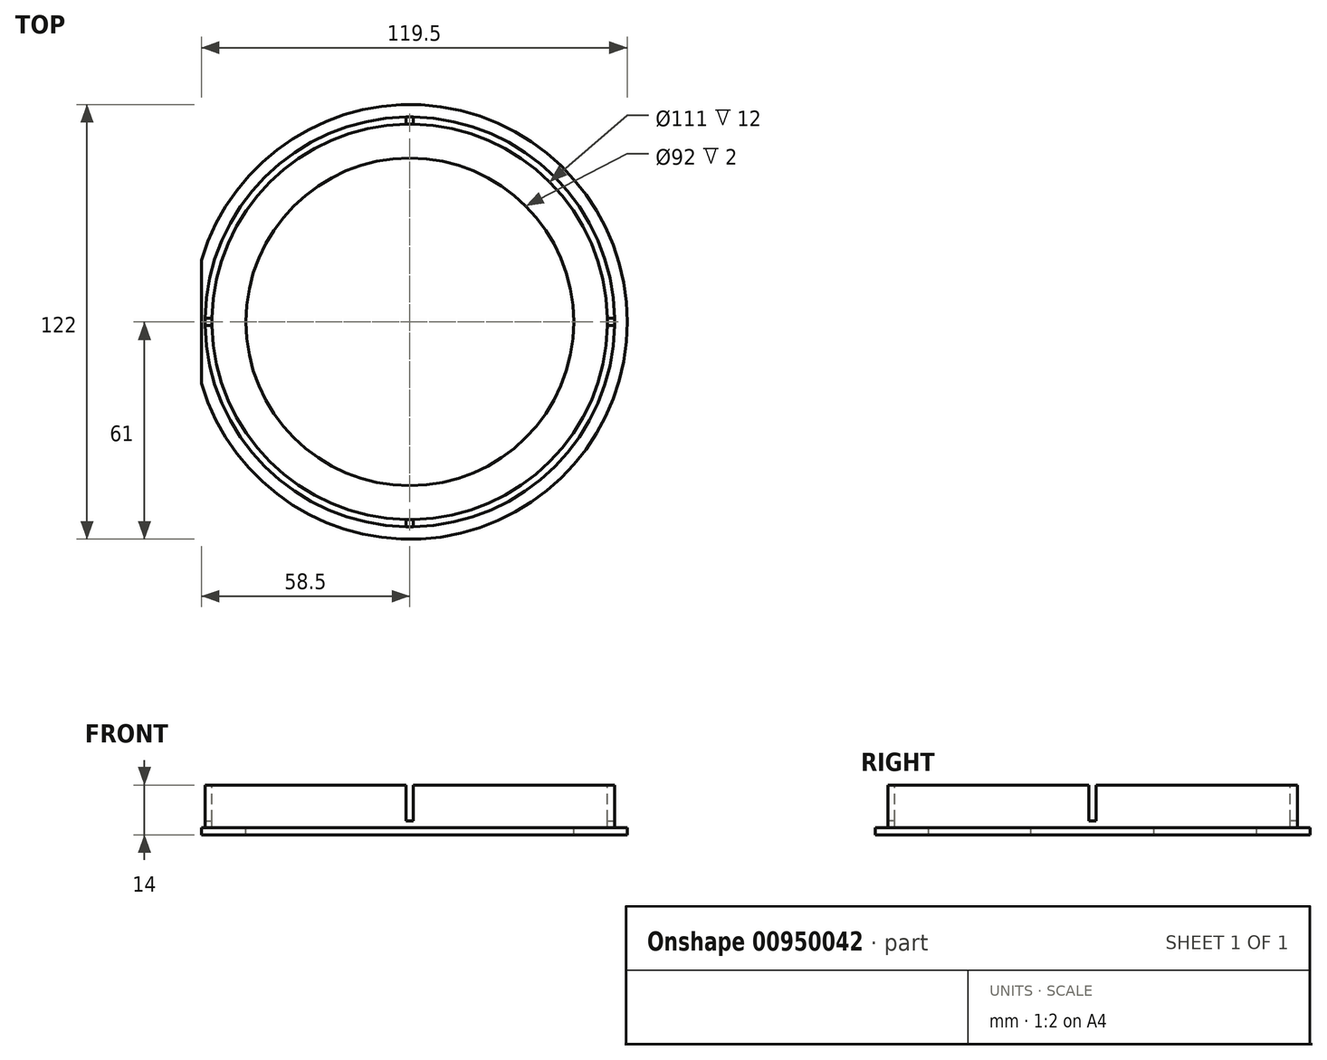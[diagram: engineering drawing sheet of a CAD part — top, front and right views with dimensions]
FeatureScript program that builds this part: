
annotation { "Feature Type Name" : "Feature", "Feature Type Description" : "" }
export const myFeature = defineFeature(function(context is Context, id is Id, definition is map)
    precondition{}
    {
        {
            var Q0;
            Q0=qCreatedBy(makeId("Top.planeOp"),FACE);
            var sketch = newSketch(context, id + "F0", { "sketchPlane" : qUnion([Q0])});
            skCircle(sketch, "E0", {"center": v(0, 0) * mm, "radius": 61 * mm});
            skSolve(sketch);
        }
        {
            var Q0;
            Q0=makeQuery(id+"F0.imprint","IMPRINT",FACE,{"disambiguationData":[TD([[makeQuery(id+"F0.imprint","IMPRINT",EDGE,{"derivedFrom":sQuery(id+"F0.wireOp",EDGE,"E0")}),1.0]])]});
            extrude(context, id + "F1", {"entities" : qUnion([Q0]), "depth" : 2 * mm, "offsetDistance" : 25 * mm});
        }
        {
            var Q0;
            Q0=makeQuery(id+"F1.opExtrude","CAP_FACE",FACE,{"disambiguationData":[OSD([sQuery(id+"F0.wireOp",EDGE,"E0")])],"isStart":false});
            var sketch = newSketch(context, id + "F2", { "sketchPlane" : qUnion([Q0])});
            skCircle(sketch, "E1", {"center": v(0, 0) * mm, "radius": 57.5 * mm});
            skSolve(sketch);
        }
        {
            var Q0;
            Q0=makeQuery(id+"F2.imprint","IMPRINT",FACE,{"disambiguationData":[TD([[makeQuery(id+"F2.imprint","IMPRINT",EDGE,{"derivedFrom":sQuery(id+"F2.wireOp",EDGE,"E1")}),1.0]])]});
            extrude(context, id + "F3", {"entities" : qUnion([Q0]), "operationType" : NewBodyOperationType.ADD, "depth" : 12 * mm, "offsetDistance" : 25 * mm});
        }
        {
            var Q0;
            Q0=makeQuery(id+"F3.opExtrude","CAP_FACE",FACE,{"disambiguationData":[OSD([sQuery(id+"F2.wireOp",EDGE,"E1")])],"isStart":false});
            var sketch = newSketch(context, id + "F4", { "sketchPlane" : qUnion([Q0])});
            skCircle(sketch, "E2", {"center": v(0, 0) * mm, "radius": 46 * mm});
            skSolve(sketch);
        }
        {
            var Q0;
            Q0=makeQuery(id+"F4.imprint","IMPRINT",FACE,{"disambiguationData":[TD([[makeQuery(id+"F4.imprint","IMPRINT",EDGE,{"derivedFrom":sQuery(id+"F4.wireOp",EDGE,"E2")}),1.0]])]});
            extrude(context, id + "F5", {"entities" : qUnion([Q0]), "operationType" : NewBodyOperationType.REMOVE, "oppositeDirection" : true, "depth" : 112.4 * mm, "offsetDistance" : 25 * mm});
        }
        {
            var Q0;
            Q0=makeQuery(id+"F3.opExtrude","CAP_FACE",FACE,{"disambiguationData":[OSD([sQuery(id+"F2.wireOp",EDGE,"E1")])],"isStart":false});
            var sketch = newSketch(context, id + "F6", { "sketchPlane" : qUnion([Q0])});
            skCircle(sketch, "E3", {"center": v(0, 0) * mm, "radius": 55.5 * mm});
            skSolve(sketch);
        }
        {
            var Q0;
            Q0=makeQuery(id+"F6.imprint","IMPRINT",FACE,{"disambiguationData":[TD([[makeQuery(id+"F6.imprint","IMPRINT",EDGE,{"derivedFrom":sQuery(id+"F6.wireOp",EDGE,"E3")}),1.0]])]});
            extrude(context, id + "F7", {"entities" : qUnion([Q0]), "operationType" : NewBodyOperationType.REMOVE, "oppositeDirection" : true, "depth" : 12 * mm, "offsetDistance" : 25 * mm});
        }
        {
            var Q0;
            Q0=makeQuery(id+"F1.opExtrude","CAP_FACE",FACE,{"disambiguationData":[OSD([sQuery(id+"F0.wireOp",EDGE,"E0")])],"isStart":false});
            var sketch = newSketch(context, id + "F8", { "sketchPlane" : qUnion([Q0])});
            skLineSegment(sketch, "E4.bottom", {"start": v(-58.5, 24.5) * mm, "end": v(58.5, 24.5) * mm});
            skLineSegment(sketch, "E4.top", {"start": v(-58.5, -24.5) * mm, "end": v(58.5, -24.5) * mm});
            skLineSegment(sketch, "E4.left", {"start": v(-58.5, 24.5) * mm, "end": v(-58.5, -24.5) * mm});
            skLineSegment(sketch, "E4.right", {"start": v(58.5, 24.5) * mm, "end": v(58.5, -24.5) * mm});
            skPoint(sketch, "E4.middle", {"position": v(0, 0) * mm});
            skSolve(sketch);
        }
        {
            var Q0;
            {var subQ0=sQuery(id+"F8.wireOp",EDGE,"E4.left");var subQ1=makeQuery(id+"F1.opExtrude","CAP_EDGE",EDGE,{"disambiguationData":[OSD([sQuery(id+"F0.wireOp",EDGE,"E0")])],"isStart":false});var subQ2=makeQuery(id+"F8.imprint","INTERSECT",VERTEX,{"disambiguationData":[OD(0.0)],"derivedFrom":[subQ1,subQ0]});Q0=makeQuery(id+"F8.imprint","IMPRINT",FACE,{"disambiguationData":[TD([[makeQuery(id+"F8.imprint","IMPRINT",EDGE,{"disambiguationData":[TD([[subQ2,-1.0]])],"derivedFrom":subQ0}),-1.0]])]});}
            extrude(context, id + "F9", {"entities" : qUnion([Q0]), "operationType" : NewBodyOperationType.REMOVE, "oppositeDirection" : true, "depth" : 25 * mm, "offsetDistance" : 25 * mm});
        }
        {
            var Q0;
            Q0=makeQuery(id+"F3.opExtrude","CAP_FACE",FACE,{"disambiguationData":[OSD([sQuery(id+"F2.wireOp",EDGE,"E1")])],"isStart":false});
            var sketch = newSketch(context, id + "F10", { "sketchPlane" : qUnion([Q0])});
            skLineSegment(sketch, "E5.bottom", {"start": v(-65.22, 1) * mm, "end": v(65.22, 1) * mm});
            skLineSegment(sketch, "E5.top", {"start": v(-65.22, -1) * mm, "end": v(65.22, -1) * mm});
            skLineSegment(sketch, "E5.left", {"start": v(-65.22, 1) * mm, "end": v(-65.22, -1) * mm});
            skLineSegment(sketch, "E5.right", {"start": v(65.22, 1) * mm, "end": v(65.22, -1) * mm});
            skPoint(sketch, "E5.middle", {"position": v(0, 0) * mm});
            skSolve(sketch);
        }
        {
            var Q0;
            Q0 = qSketchRegion(id + "F10", true);
            extrude(context, id + "F11", {"entities" : qUnion([Q0]), "operationType" : NewBodyOperationType.REMOVE, "oppositeDirection" : true, "depth" : 10 * mm, "offsetDistance" : 25 * mm});
        }
        {
            var Q0;
            {var subQ0=sQuery(id+"F2.wireOp",EDGE,"E1");Q0=makeQuery(id+"F11.boolean.opBoolean","SPLIT",FACE,{"disambiguationData":[TD([makeQuery(id+"F11.opExtrude","SWEPT_FACE",FACE,{"disambiguationData":[OSD([sQuery(id+"F10.wireOp",EDGE,"E5.bottom")])]})])],"derivedFrom":makeQuery(id+"F3.opExtrude","CAP_FACE",FACE,{"disambiguationData":[OSD([subQ0])],"isStart":false})});}
            var sketch = newSketch(context, id + "F12", { "sketchPlane" : qUnion([Q0])});
            skLineSegment(sketch, "E6.bottom", {"start": v(-1, 59.5) * mm, "end": v(1, 59.5) * mm});
            skLineSegment(sketch, "E6.top", {"start": v(-1, -59.5) * mm, "end": v(1, -59.5) * mm});
            skLineSegment(sketch, "E6.left", {"start": v(-1, 59.5) * mm, "end": v(-1, -59.5) * mm});
            skLineSegment(sketch, "E6.right", {"start": v(1, 59.5) * mm, "end": v(1, -59.5) * mm});
            skPoint(sketch, "E6.middle", {"position": v(0, 0) * mm});
            skSolve(sketch);
        }
        {
            var Q0;
            Q0 = qSketchRegion(id + "F12", true);
            extrude(context, id + "F13", {"entities" : qUnion([Q0]), "operationType" : NewBodyOperationType.REMOVE, "oppositeDirection" : true, "depth" : 10 * mm, "offsetDistance" : 25 * mm});
        }
    });
